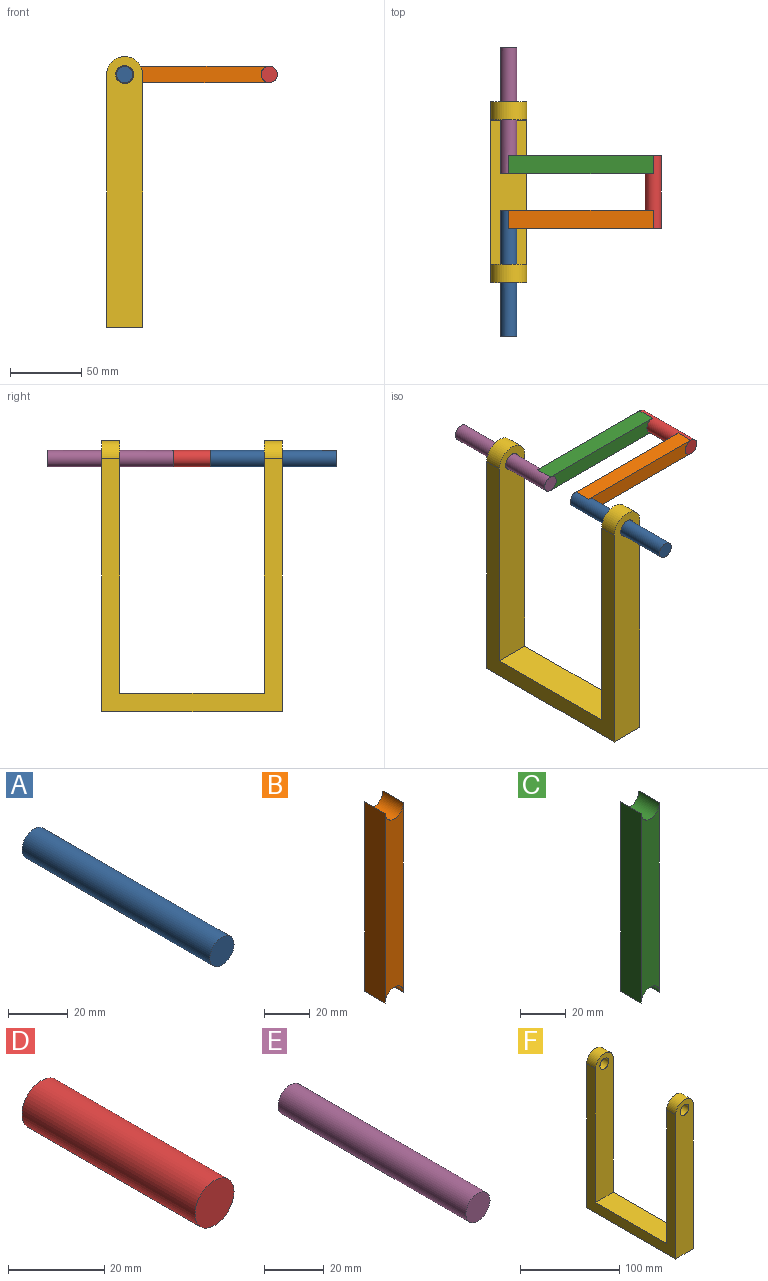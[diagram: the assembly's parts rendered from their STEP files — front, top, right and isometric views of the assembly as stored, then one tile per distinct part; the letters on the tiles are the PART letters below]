
ASSEMBLY  parts=6 mates=5
PART A: 3 faces, bbox 11.4x88.9x11.4 mm
  f0: cylinder r=5.71mm len=88.9mm, axis (0,1,0), area 3192.3mm2, adj f1,f2
  f1: plane 11.43x11.43mm, normal (0,1,0), area 102.6mm2, adj f0
  f2: plane 11.43x11.43mm, normal (0,-1,0), area 102.6mm2, adj f0
PART B: 6 faces, bbox 11.4x12.7x101.6 mm
  f0: plane 101.59x12.7mm, normal (1,0,0), area 1290.2mm2, adj f2,f3,f4,f5
  f1: plane 101.59x12.7mm, normal (-1,0,0), area 1290.2mm2, adj f2,f3,f4,f5
  f2: plane 101.59x11.43mm, normal (0,-1,0), area 1058.5mm2, adj f0,f1,f4,f5
  f3: plane 101.59x11.43mm, normal (0,1,0), area 1058.5mm2, adj f0,f1,f4,f5
  f4: cylinder r=5.71mm len=12.7mm, axis (0,1,0), area 228mm2, adj f0,f1,f2,f3
  f5: cylinder r=5.71mm len=12.7mm, axis (0,-1,0), area 228mm2, adj f0,f1,f2,f3
PART C: 6 faces, bbox 11.4x12.7x101.6 mm
  f0: plane 101.59x12.7mm, normal (-1,0,0), area 1290.2mm2, adj f2,f3,f4,f5
  f1: plane 101.59x12.7mm, normal (1,0,0), area 1290.2mm2, adj f2,f3,f4,f5
  f2: cylinder r=5.71mm len=12.7mm, axis (0,-1,0), area 228mm2, adj f0,f1,f3,f4
  f3: plane 101.59x11.43mm, normal (0,1,0), area 1058.5mm2, adj f0,f1,f2,f5
  f4: plane 101.59x11.43mm, normal (0,-1,0), area 1058.5mm2, adj f0,f1,f2,f5
  f5: cylinder r=5.71mm len=12.7mm, axis (0,-1,0), area 228mm2, adj f0,f1,f3,f4
PART D: 3 faces, bbox 11.4x50.8x11.4 mm
  f0: cylinder r=5.71mm len=50.8mm, axis (0,1,0), area 1824.1mm2, adj f1,f2
  f1: plane 11.43x11.43mm, normal (0,-1,0), area 102.6mm2, adj f0
  f2: plane 11.43x11.43mm, normal (0,1,0), area 102.6mm2, adj f0
PART E: 3 faces, bbox 11.4x88.9x11.4 mm
  f0: plane 11.43x11.43mm, normal (0,-1,0), area 102.6mm2, adj f1
  f1: cylinder r=5.71mm len=88.9mm, axis (0,1,0), area 3192.3mm2, adj f0,f2
  f2: plane 11.43x11.43mm, normal (0,1,0), area 102.6mm2, adj f1
PART F: 12 faces, bbox 25.4x127x190.5 mm
  f0: cylinder r=12.7mm len=25.4mm, axis (0,1,0), area 506.7mm2, adj f2,f5,f7,f9
  f1: cylinder r=12.7mm len=25.4mm, axis (0,1,0), area 506.7mm2, adj f2,f5,f8,f10
  f2: plane 177.8x127mm, normal (-1,0,0), area 5806.4mm2, adj f0,f1,f4,f7,f8,f9,f10,f11
  f3: cylinder r=6.35mm len=12.7mm, axis (0,1,0), area 506.7mm2, adj f7,f9
  f4: plane 127x25.4mm, normal (0,0,-1), area 3225.8mm2, adj f2,f5,f7,f8
  f5: plane 177.8x127mm, normal (1,0,0), area 5806.4mm2, adj f0,f1,f4,f7,f8,f9,f10,f11
  f6: cylinder r=6.35mm len=12.7mm, axis (0,1,0), area 506.7mm2, adj f8,f10
  f7: plane 190.5x25.4mm, normal (0,-1,0), area 4642.8mm2, adj f0,f2,f3,f4,f5
  f8: plane 190.5x25.4mm, normal (0,1,0), area 4642.8mm2, adj f1,f2,f4,f5,f6
  f9: plane 177.8x25.4mm, normal (0,1,0), area 4320.2mm2, adj f0,f2,f3,f5,f11
  f10: plane 177.8x25.4mm, normal (0,-1,0), area 4320.2mm2, adj f1,f2,f5,f6,f11
  f11: plane 101.6x25.4mm, normal (0,0,1), area 2580.6mm2, adj f2,f5,f9,f10
PLACE A rot(axis=(-1,0,0),180deg) t=(-45.5,-28.91,-22.95)mm
PLACE B rot(axis=(-0.71,0,-0.71),180deg) t=(56.04,-28.91,78.68)mm
PLACE C rot(axis=(0.71,0,0.71),180deg) t=(56.04,-28.91,78.68)mm
PLACE D rot(axis=(-0.71,0,-0.71),180deg) t=(56.04,-28.91,78.68)mm
PLACE E rot(axis=(0.71,0,0.71),180deg) t=(56.04,-28.91,78.68)mm
PLACE F t=(-45.54,-28.91,2.43)mm fixed
MATE cylindrical F.f0 <-> E.f1  axis (0,-1,0) through (-45.54,21.89,78.63)mm
MATE fastened E.f1 <-> C.f5  axis (0,-1,0) through (-45.54,-16.21,78.63)mm
MATE fastened D.f0 <-> C.f2  axis (0,1,0) through (56.04,-3.51,78.68)mm
MATE fastened B.f4 <-> D.f0  axis (0,-1,0) through (56.04,-54.31,78.68)mm
MATE fastened A.f0 <-> B.f5  axis (0,1,0) through (-45.54,-41.61,78.63)mm
